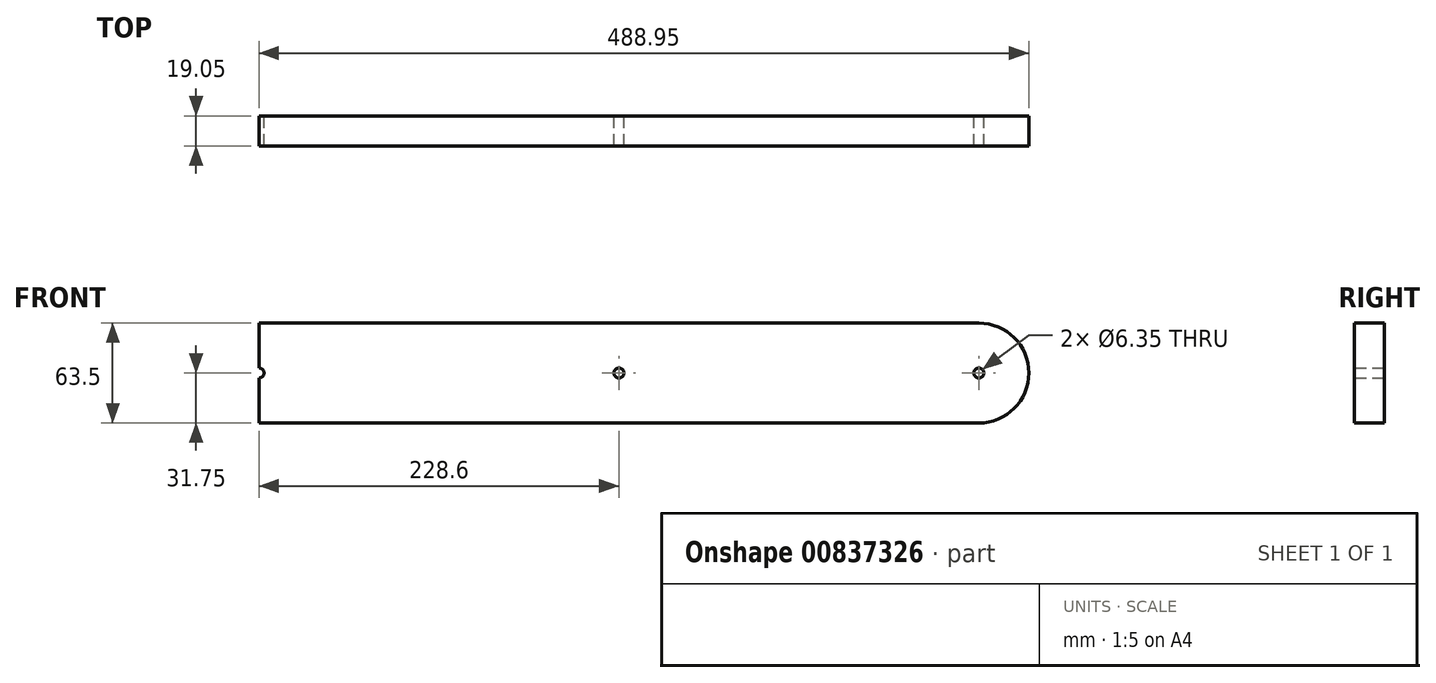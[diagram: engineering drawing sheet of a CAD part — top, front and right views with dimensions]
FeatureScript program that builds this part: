
annotation { "Feature Type Name" : "Feature", "Feature Type Description" : "" }
export const myFeature = defineFeature(function(context is Context, id is Id, definition is map)
    precondition{}
    {
        {
            var Q0;
            Q0=qCreatedBy(makeId("Front.planeOp"),FACE);
            var sketch = newSketch(context, id + "F0", { "sketchPlane" : qUnion([Q0])});
            skArc(sketch, "E0", {"start": v(0, -31.75) * mm, "mid": v(-31.75, 0) * mm, "end": v(0, 31.75) * mm});
            skLineSegment(sketch, "E1.bottom", {"start": v(0, -31.75) * mm, "end": v(457.2, -31.75) * mm});
            skLineSegment(sketch, "E1.top", {"start": v(0, 31.75) * mm, "end": v(457.2, 31.75) * mm});
            skLineSegment(sketch, "E1.left", {"start": v(0, -31.75) * mm, "end": v(0, 31.75) * mm});
            skLineSegment(sketch, "E1.right", {"start": v(457.2, -31.75) * mm, "end": v(457.2, 31.75) * mm});
            skArc(sketch, "E2", {"start": v(457.2, -31.75) * mm, "mid": v(488.95, 0) * mm, "end": v(457.2, 31.75) * mm});
            skSolve(sketch);
        }
        {
            var Q0;
            Q0=makeQuery(id+"F0.imprint","IMPRINT",FACE,{"disambiguationData":[TD([[makeQuery(id+"F0.imprint","IMPRINT",EDGE,{"derivedFrom":sQuery(id+"F0.wireOp",EDGE,"E1.bottom")}),1.0]])]});
            var Q1;
            Q1=makeQuery(id+"F0.imprint","IMPRINT",FACE,{"disambiguationData":[TD([[makeQuery(id+"F0.imprint","IMPRINT",EDGE,{"derivedFrom":sQuery(id+"F0.wireOp",EDGE,"E0")}),-1.0]])]});
            var Q2;
            Q2=makeQuery(id+"F0.imprint","IMPRINT",FACE,{"disambiguationData":[TD([[makeQuery(id+"F0.imprint","IMPRINT",EDGE,{"derivedFrom":sQuery(id+"F0.wireOp",EDGE,"E1.right")}),-1.0]])]});
            extrude(context, id + "F1", {"entities" : qUnion([Q0, Q1, Q2]), "depth" : 19.05 * mm, "offsetDistance" : 25.4 * mm});
        }
        {
            var Q0;
            Q0=makeQuery(id+"F1.opExtrude","CAP_FACE",FACE,{"disambiguationData":[OSD([sQuery(id+"F0.wireOp",EDGE,"E0"),sQuery(id+"F0.wireOp",EDGE,"E1.bottom"),sQuery(id+"F0.wireOp",EDGE,"E1.top"),sQuery(id+"F0.wireOp",EDGE,"E2")])],"isStart":true});
            var sketch = newSketch(context, id + "F2", { "sketchPlane" : qUnion([Q0])});
            skPoint(sketch, "E3", {"position": v(-457.2, 0) * mm});
            skPoint(sketch, "E4", {"position": v(0, 0) * mm});
            skPoint(sketch, "E5", {"position": v(-228.6, 0) * mm});
            skLineSegment(sketch, "E6", {"start": v(-457.2, 0) * mm, "end": v(0, 0) * mm});
            skSolve(sketch);
        }
        {
            var Q0;
            Q0=sQuery(id+"F2.wireOp",VERTEX,"E3");
            var Q1;
            Q1=sQuery(id+"F2.wireOp",VERTEX,"E4");
            var Q2;
            Q2=sQuery(id+"F2.wireOp",VERTEX,"E5");
            var Q3;
            Q3=makeQuery(id+"F1.opExtrude","SWEPT_BODY",BODY,{"disambiguationData":[OSD([sQuery(id+"F0.wireOp",EDGE,"E0"),sQuery(id+"F0.wireOp",EDGE,"E1.bottom"),sQuery(id+"F0.wireOp",EDGE,"E1.top"),sQuery(id+"F0.wireOp",EDGE,"E2")])]});
            hole(context, id + "F3", {"style" : HoleStyle.SIMPLE, "endStyle" : HoleEndStyle.THROUGH, "holeDiameter" : 6.35 * mm, "majorDiameter" : 6.35 * mm, "isTappedThrough" : true, "tappedDepth" : 12.7 * mm, "tapClearance" : 3, "locations" : qUnion([Q0, Q1, Q2]), "scope" : qUnion([Q3])});
        }
    });
